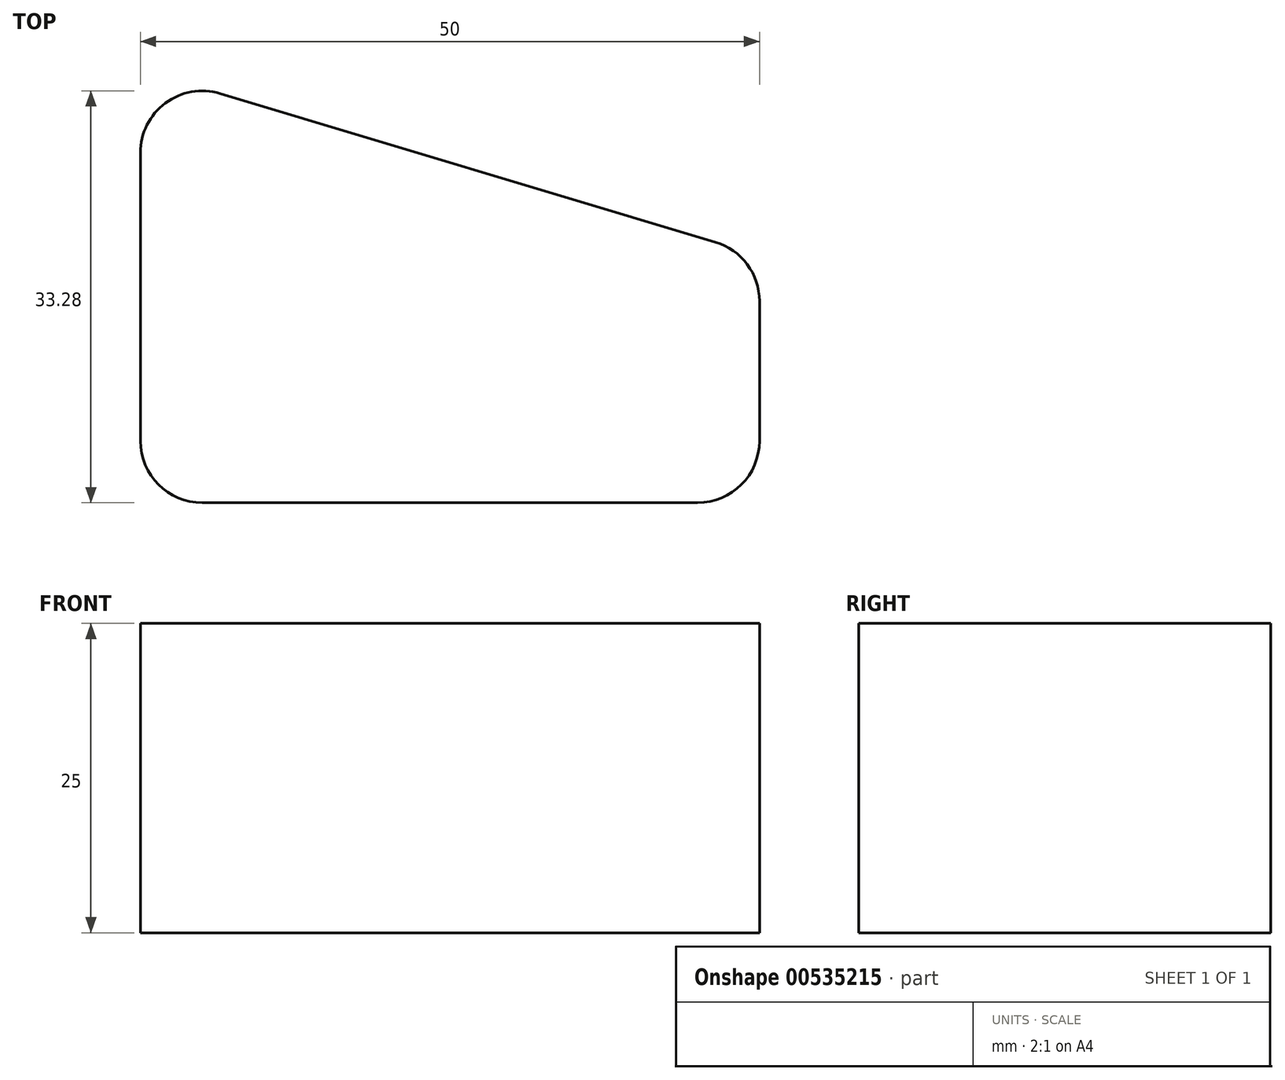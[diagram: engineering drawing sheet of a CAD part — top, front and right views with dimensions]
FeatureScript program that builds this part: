
annotation { "Feature Type Name" : "Feature", "Feature Type Description" : "" }
export const myFeature = defineFeature(function(context is Context, id is Id, definition is map)
    precondition{}
    {
        {
            var Q0;
            Q0=qCreatedBy(makeId("Top.planeOp"),FACE);
            var sketch = newSketch(context, id + "F0", { "sketchPlane" : qUnion([Q0])});
            skLineSegment(sketch, "E0", {"start": v(-45, 0) * mm, "end": v(-5, 0) * mm});
            skLineSegment(sketch, "E1", {"start": v(0, 5) * mm, "end": v(0, 16.28) * mm});
            skLineSegment(sketch, "E2", {"start": v(-3.56, 21.07) * mm, "end": v(-43.56, 33.07) * mm});
            skLineSegment(sketch, "E3", {"start": v(-50, 28.28) * mm, "end": v(-50, 5) * mm});
            skPoint(sketch, "E4.visualSharp", {"position": v(-50, 35) * mm});
            skArc(sketch, "E4.filletArc", {"start": v(-43.56, 33.07) * mm, "mid": v(-47.98, 32.3) * mm, "end": v(-50, 28.28) * mm});
            skPoint(sketch, "E5.visualSharp", {"position": v(0, 20) * mm});
            skArc(sketch, "E5.filletArc", {"start": v(0, 16.28) * mm, "mid": v(-0.99, 19.26) * mm, "end": v(-3.56, 21.07) * mm});
            skPoint(sketch, "E6.visualSharp", {"position": v(0, 0) * mm});
            skArc(sketch, "E6.filletArc", {"start": v(-5, 0) * mm, "mid": v(-1.46, 1.46) * mm, "end": v(0, 5) * mm});
            skPoint(sketch, "E7.visualSharp", {"position": v(-50, 0) * mm});
            skArc(sketch, "E7.filletArc", {"start": v(-50, 5) * mm, "mid": v(-48.54, 1.46) * mm, "end": v(-45, 0) * mm});
            skSolve(sketch);
        }
        {
            var Q0;
            Q0 = qSketchRegion(id + "F0", true);
            extrude(context, id + "F1", {"entities" : qUnion([Q0]), "depth" : 25 * mm, "offsetDistance" : 25 * mm});
        }
    });
